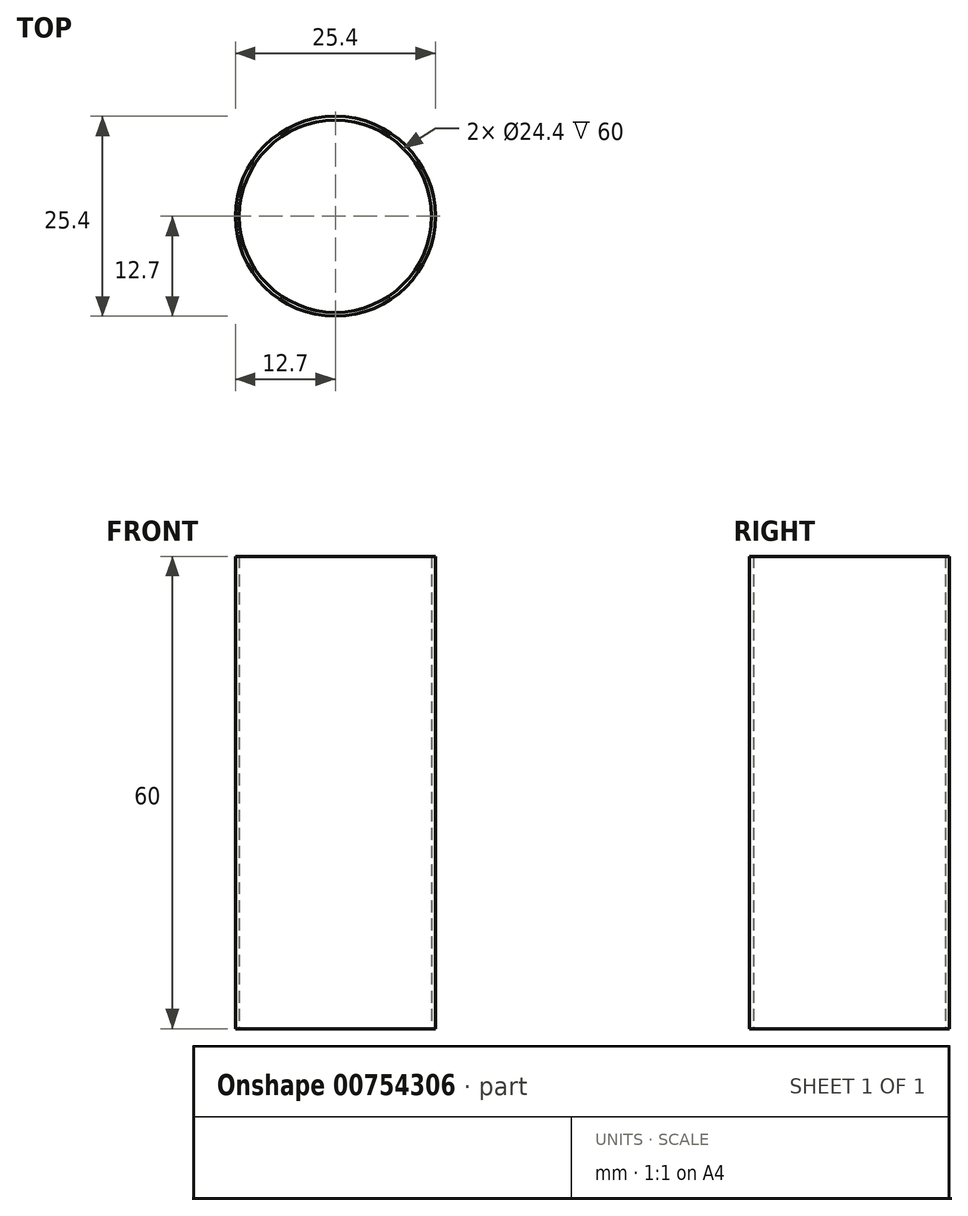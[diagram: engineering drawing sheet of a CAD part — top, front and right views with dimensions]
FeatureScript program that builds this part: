
annotation { "Feature Type Name" : "Feature", "Feature Type Description" : "" }
export const myFeature = defineFeature(function(context is Context, id is Id, definition is map)
    precondition{}
    {
        {
            var Q0;
            Q0=qCreatedBy(makeId("Top.planeOp"),FACE);
            var sketch = newSketch(context, id + "F0", { "sketchPlane" : qUnion([Q0])});
            skCircle(sketch, "E0", {"center": v(0, 0) * mm, "radius": 12.7 * mm});
            skCircle(sketch, "E1", {"center": v(0, 0) * mm, "radius": 12.2 * mm});
            skSolve(sketch);
        }
        {
            var Q0;
            Q0=makeQuery(id+"F0.imprint","IMPRINT",FACE,{"disambiguationData":[TD([[makeQuery(id+"F0.imprint","IMPRINT",EDGE,{"derivedFrom":sQuery(id+"F0.wireOp",EDGE,"E0")}),1.0]])]});
            extrude(context, id + "F1", {"entities" : qUnion([Q0]), "depth" : 60 * mm, "offsetDistance" : 25 * mm});
        }
    });
